annotation { "Feature Type Name" : "Feature", "Feature Type Description" : "" }
export const myFeature = defineFeature(function(context is Context, id is Id, definition is map)
    precondition{}
    {
        {
            var Q0;
            Q0=qCreatedBy(makeId("Top.planeOp"),FACE);
            var sketch = newSketch(context, id + "F0", { "sketchPlane" : qUnion([Q0])});
            skCircle(sketch, "E0", {"center": v(0, 0) * mm, "radius": 127 * mm});
            skSolve(sketch);
        }
        {
            var Q0;
            Q0 = qSketchRegion(id + "F0", true);
            extrude(context, id + "F1", {"entities" : qUnion([Q0]), "depth" : 63.5 * mm});
        }
        {
            var Q0;
            Q0=makeQuery(id+"F1.opExtrude","CAP_FACE",FACE,{"disambiguationData":[OSD([sQuery(id+"F0.wireOp",EDGE,"E0")])],"isStart":false});
            var sketch = newSketch(context, id + "F2", { "sketchPlane" : qUnion([Q0])});
            skCircle(sketch, "E1", {"center": v(0, 0) * mm, "radius": 107.95 * mm});
            skSolve(sketch);
        }
        {
            var Q0;
            Q0=makeQuery(id+"F2.imprint","IMPRINT",FACE,{"disambiguationData":[TD([[makeQuery(id+"F2.imprint","IMPRINT",EDGE,{"derivedFrom":sQuery(id+"F2.wireOp",EDGE,"E1")}),1.0]])]});
            extrude(context, id + "F3", {"entities" : qUnion([Q0]), "operationType" : NewBodyOperationType.REMOVE, "oppositeDirection" : true, "depth" : 254 * mm});
        }
        {
            var Q0;
            Q0=qCreatedBy(makeId("Front.planeOp"),FACE);
            var sketch = newSketch(context, id + "F4", { "sketchPlane" : qUnion([Q0])});
            skLineSegment(sketch, "E2", {"start": v(0, 0) * mm, "end": v(0, 63.5) * mm});
            skLineSegment(sketch, "E3", {"start": v(-127.9, 31.75) * mm, "end": v(134.22, 31.75) * mm});
            skSolve(sketch);
        }
        {
            var Q0;
            Q0=qCreatedBy(makeId("Front.planeOp"),FACE);
            var sketch = newSketch(context, id + "F5", { "sketchPlane" : qUnion([Q0])});
            skCircle(sketch, "E4.cCircle", {"center": v(0, 47.62) * mm, "radius": 12.7 * mm, "construction": true});
            skLineSegment(sketch, "E4.0", {"start": v(12.7, 47.62) * mm, "end": v(6.35, 36.63) * mm});
            skLineSegment(sketch, "E4.1", {"start": v(6.35, 36.63) * mm, "end": v(-6.35, 36.63) * mm});
            skLineSegment(sketch, "E4.2", {"start": v(-6.35, 36.63) * mm, "end": v(-12.7, 47.62) * mm});
            skLineSegment(sketch, "E4.3", {"start": v(-12.7, 47.62) * mm, "end": v(-6.35, 58.62) * mm});
            skLineSegment(sketch, "E4.4", {"start": v(-6.35, 58.62) * mm, "end": v(6.35, 58.62) * mm});
            skLineSegment(sketch, "E4.5", {"start": v(6.35, 58.62) * mm, "end": v(12.7, 47.62) * mm});
            skLineSegment(sketch, "E5.direction1", {"start": v(-6.35, 36.63) * mm, "end": v(6.35, 36.63) * mm, "construction": true});
            skPoint(sketch, "E6.orphan", {"position": v(17.46, 60.96) * mm});
            skPoint(sketch, "E7.orphan", {"position": v(9.53, 47.21) * mm});
            skPoint(sketch, "E8.orphan", {"position": v(33.34, 33.46) * mm});
            skPoint(sketch, "E9.orphan", {"position": v(41.27, 47.21) * mm});
            skPoint(sketch, "E10.orphan", {"position": v(15.87, 28.8) * mm});
            skLineSegment(sketch, "E11", {"start": v(66.67, 47.21) * mm, "end": v(66.67, 47.21) * mm});
            skPoint(sketch, "E12.orphan", {"position": v(33.34, 42.55) * mm});
            skPoint(sketch, "E13.orphan", {"position": v(9.53, 28.8) * mm});
            skLineSegment(sketch, "E14.0.1.0", {"start": v(-6.35, 4.88) * mm, "end": v(-12.7, 15.88) * mm});
            skLineSegment(sketch, "E14.0.1.1", {"start": v(-12.7, 15.88) * mm, "end": v(-6.35, 26.87) * mm});
            skLineSegment(sketch, "E14.0.1.2", {"start": v(-6.35, 26.87) * mm, "end": v(6.35, 26.87) * mm});
            skLineSegment(sketch, "E14.0.1.3", {"start": v(6.35, 26.87) * mm, "end": v(12.7, 15.87) * mm});
            skLineSegment(sketch, "E14.0.1.4", {"start": v(12.7, 15.88) * mm, "end": v(6.35, 4.88) * mm});
            skLineSegment(sketch, "E14.0.1.5", {"start": v(6.35, 4.88) * mm, "end": v(-6.35, 4.88) * mm});
            skLineSegment(sketch, "E14.direction1", {"start": v(-12.7, 47.62) * mm, "end": v(9.53, 47.62) * mm, "construction": true});
            skLineSegment(sketch, "E14.direction2", {"start": v(-12.7, 47.62) * mm, "end": v(-12.7, 15.88) * mm, "construction": true});
            skSolve(sketch);
        }
        {
            var Q0;
            Q0 = qSketchRegion(id + "F5", true);
            extrude(context, id + "F6", {"entities" : qUnion([Q0]), "operationType" : NewBodyOperationType.REMOVE, "endBound" : BoundingType.THROUGH_ALL, "depth" : 25.4 * mm});
        }
        {
            var Q0;
            Q0=makeQuery(id+"F6.boolean.opBoolean","COPY",FACE,{"derivedFrom":makeQuery(id+"F6.opExtrude","SWEPT_FACE",FACE,{"disambiguationData":[OSD([sQuery(id+"F5.wireOp",EDGE,"E4.0")])]})});
            var Q1;
            Q1=makeQuery(id+"F6.boolean.opBoolean","COPY",FACE,{"derivedFrom":makeQuery(id+"F6.opExtrude","SWEPT_FACE",FACE,{"disambiguationData":[OSD([sQuery(id+"F5.wireOp",EDGE,"E4.5")])]})});
            var Q2;
            Q2=makeQuery(id+"F6.boolean.opBoolean","COPY",FACE,{"derivedFrom":makeQuery(id+"F6.opExtrude","SWEPT_FACE",FACE,{"disambiguationData":[OSD([sQuery(id+"F5.wireOp",EDGE,"E14.0.1.3")])]})});
            var Q3;
            Q3=makeQuery(id+"F6.boolean.opBoolean","COPY",FACE,{"derivedFrom":makeQuery(id+"F6.opExtrude","SWEPT_FACE",FACE,{"disambiguationData":[OSD([sQuery(id+"F5.wireOp",EDGE,"E14.0.1.4")])]})});
            var Q4;
            Q4=makeQuery(id+"F6.boolean.opBoolean","COPY",FACE,{"derivedFrom":makeQuery(id+"F6.opExtrude","SWEPT_FACE",FACE,{"disambiguationData":[OSD([sQuery(id+"F5.wireOp",EDGE,"E4.1")])]})});
            var Q5;
            Q5=makeQuery(id+"F6.boolean.opBoolean","COPY",FACE,{"derivedFrom":makeQuery(id+"F6.opExtrude","SWEPT_FACE",FACE,{"disambiguationData":[OSD([sQuery(id+"F5.wireOp",EDGE,"E4.2")])]})});
            var Q6;
            Q6=makeQuery(id+"F6.boolean.opBoolean","COPY",FACE,{"derivedFrom":makeQuery(id+"F6.opExtrude","SWEPT_FACE",FACE,{"disambiguationData":[OSD([sQuery(id+"F5.wireOp",EDGE,"E4.3")])]})});
            var Q7;
            Q7=makeQuery(id+"F6.boolean.opBoolean","COPY",FACE,{"derivedFrom":makeQuery(id+"F6.opExtrude","SWEPT_FACE",FACE,{"disambiguationData":[OSD([sQuery(id+"F5.wireOp",EDGE,"E14.0.1.0")])]})});
            var Q8;
            Q8=makeQuery(id+"F6.boolean.opBoolean","COPY",FACE,{"derivedFrom":makeQuery(id+"F6.opExtrude","SWEPT_FACE",FACE,{"disambiguationData":[OSD([sQuery(id+"F5.wireOp",EDGE,"E14.0.1.1")])]})});
            var Q9;
            Q9=makeQuery(id+"F6.boolean.opBoolean","COPY",FACE,{"derivedFrom":makeQuery(id+"F6.opExtrude","SWEPT_FACE",FACE,{"disambiguationData":[OSD([sQuery(id+"F5.wireOp",EDGE,"E14.0.1.5")])]})});
            var Q10;
            Q10=makeQuery(id+"F6.boolean.opBoolean","COPY",FACE,{"derivedFrom":makeQuery(id+"F6.opExtrude","SWEPT_FACE",FACE,{"disambiguationData":[OSD([sQuery(id+"F5.wireOp",EDGE,"E14.0.1.2")])]})});
            var Q11;
            Q11=makeQuery(id+"F6.boolean.opBoolean","COPY",FACE,{"derivedFrom":makeQuery(id+"F6.opExtrude","SWEPT_FACE",FACE,{"disambiguationData":[OSD([sQuery(id+"F5.wireOp",EDGE,"E4.4")])]})});
            var Q12;
            Q12=sQuery(id+"F4.wireOp",EDGE,"E2");
            circularPattern(context, id + "F7", {"patternType" : PatternType.FACE, "faces" : qUnion([Q0, Q1, Q2, Q3, Q4, Q5, Q6, Q7, Q8, Q9, Q10, Q11]), "axis" : qUnion([Q12]), "angle" : 360 * degree, "instanceCount" : 14, "equalSpace" : true});
        }
        {
            var Q0;
            Q0=makeQuery(id+"F1.opExtrude","CAP_FACE",FACE,{"disambiguationData":[OSD([sQuery(id+"F0.wireOp",EDGE,"E0")])],"isStart":false});
            var Q1;
            Q1=makeQuery(id+"F1.opExtrude","CAP_FACE",FACE,{"disambiguationData":[OSD([sQuery(id+"F0.wireOp",EDGE,"E0")])],"isStart":true});
            cPlane(context, id + "F8", {"entities" : qUnion([Q0, Q1]), "cplaneType" : CPlaneType.MID_PLANE, "offset" : 25.4 * mm, "width" : 152.4 * mm, "height" : 152.4 * mm});
        }
        {
            var Q0;
            Q0=qCreatedBy(id+"F8.planeOp",FACE);
            var sketch = newSketch(context, id + "F9", { "sketchPlane" : qUnion([Q0])});
            skCircle(sketch, "E15", {"center": v(0, 0) * mm, "radius": 120.06 * mm});
            skLineSegment(sketch, "E16", {"start": v(0, 0) * mm, "end": v(190.3, 0) * mm});
            skLineSegment(sketch, "E17", {"start": v(190.3, 0) * mm, "end": v(0, 0) * mm});
            skLineSegment(sketch, "E18", {"start": v(169.78, 81.76) * mm, "end": v(0, 0) * mm});
            skLineSegment(sketch, "E19", {"start": v(108.17, 52.1) * mm, "end": v(89.15, 91.6) * mm});
            skPoint(sketch, "E20", {"position": v(108.17, 52.1) * mm});
            skSolve(sketch);
        }
        {
            var Q0;
            Q0=sQuery(id+"F9.wireOp",VERTEX,"E20");
            var Q1;
            Q1=sQuery(id+"F9.wireOp",EDGE,"E18");
            cPlane(context, id + "F10", {"entities" : qUnion([Q0, Q1]), "cplaneType" : CPlaneType.LINE_POINT, "offset" : 25.4 * mm, "width" : 152.4 * mm, "height" : 152.4 * mm});
        }
        {
            var Q0;
            Q0=qCreatedBy(id+"F10.planeOp",FACE);
            var sketch = newSketch(context, id + "F11", { "sketchPlane" : qUnion([Q0])});
            skCircle(sketch, "E21.cCircle", {"center": v(0, 31.75) * mm, "radius": 12.7 * mm, "construction": true});
            skLineSegment(sketch, "E21.0", {"start": v(-12.7, 31.75) * mm, "end": v(-6.35, 42.75) * mm});
            skLineSegment(sketch, "E21.1", {"start": v(-6.35, 42.75) * mm, "end": v(6.35, 42.75) * mm});
            skLineSegment(sketch, "E21.2", {"start": v(6.35, 42.75) * mm, "end": v(12.7, 31.75) * mm});
            skLineSegment(sketch, "E21.3", {"start": v(12.7, 31.75) * mm, "end": v(6.35, 20.75) * mm});
            skLineSegment(sketch, "E21.4", {"start": v(6.35, 20.75) * mm, "end": v(-6.35, 20.75) * mm});
            skLineSegment(sketch, "E21.5", {"start": v(-6.35, 20.75) * mm, "end": v(-12.7, 31.75) * mm});
            skLineSegment(sketch, "E22.0.1.0", {"start": v(-6.35, 74.5) * mm, "end": v(6.35, 74.5) * mm, "construction": true});
            skLineSegment(sketch, "E22.0.1.1", {"start": v(-12.7, 63.5) * mm, "end": v(-6.35, 74.5) * mm, "construction": true});
            skLineSegment(sketch, "E22.0.1.2", {"start": v(-6.35, 52.5) * mm, "end": v(-9.88, 58.62) * mm});
            skLineSegment(sketch, "E22.0.1.3", {"start": v(6.35, 52.5) * mm, "end": v(-6.35, 52.5) * mm});
            skLineSegment(sketch, "E22.0.1.4", {"start": v(9.88, 58.62) * mm, "end": v(6.35, 52.5) * mm});
            skLineSegment(sketch, "E22.0.1.5", {"start": v(6.35, 74.5) * mm, "end": v(12.7, 63.5) * mm, "construction": true});
            skLineSegment(sketch, "E22.direction1", {"start": v(-6.35, 42.75) * mm, "end": v(17.46, 42.75) * mm, "construction": true});
            skLineSegment(sketch, "E22.direction2", {"start": v(-6.35, 42.75) * mm, "end": v(-6.35, 74.5) * mm, "construction": true});
            skLineSegment(sketch, "E23.0.1.0", {"start": v(6.35, 11) * mm, "end": v(9.88, 4.88) * mm});
            skLineSegment(sketch, "E23.0.1.1", {"start": v(-9.88, 4.88) * mm, "end": v(-6.35, 11) * mm});
            skLineSegment(sketch, "E23.direction1", {"start": v(12.7, 31.75) * mm, "end": v(41.27, 31.75) * mm, "construction": true});
            skLineSegment(sketch, "E23.direction2", {"start": v(12.7, 31.75) * mm, "end": v(12.7, 0) * mm, "construction": true});
            skLineSegment(sketch, "E24", {"start": v(6.35, 11) * mm, "end": v(-6.35, 11) * mm});
            skLineSegment(sketch, "E25", {"start": v(9.88, 58.62) * mm, "end": v(-9.88, 58.62) * mm});
            skLineSegment(sketch, "E26", {"start": v(9.88, 4.88) * mm, "end": v(-9.88, 4.88) * mm});
            skSolve(sketch);
        }
        {
            var Q0;
            Q0=qCreatedBy(makeId("Front.planeOp"),FACE);
            var sketch = newSketch(context, id + "F12", { "sketchPlane" : qUnion([Q0])});
            skLineSegment(sketch, "E27", {"start": v(145.81, 63.5) * mm, "end": v(145.81, 63.5) * mm});
            skLineSegment(sketch, "E28", {"start": v(0, 0) * mm, "end": v(0, 93.67) * mm, "construction": true});
            skSolve(sketch);
        }
        {
            var Q0;
            Q0 = qSketchRegion(id + "F11", true);
            extrude(context, id + "F13", {"entities" : qUnion([Q0]), "operationType" : NewBodyOperationType.REMOVE, "endBound" : BoundingType.SYMMETRIC, "depth" : 381 * mm});
        }
        {
            var Q0;
            Q0=makeQuery(id+"F13.boolean.opBoolean","COPY",FACE,{"derivedFrom":makeQuery(id+"F13.opExtrude","SWEPT_FACE",FACE,{"disambiguationData":[OSD([sQuery(id+"F11.wireOp",EDGE,"E21.3")])]})});
            var Q1;
            Q1=makeQuery(id+"F13.boolean.opBoolean","COPY",FACE,{"derivedFrom":makeQuery(id+"F13.opExtrude","SWEPT_FACE",FACE,{"disambiguationData":[OSD([sQuery(id+"F11.wireOp",EDGE,"E21.2")])]})});
            var Q2;
            Q2=makeQuery(id+"F13.boolean.opBoolean","COPY",FACE,{"derivedFrom":makeQuery(id+"F13.opExtrude","SWEPT_FACE",FACE,{"disambiguationData":[OSD([sQuery(id+"F11.wireOp",EDGE,"E22.0.1.4")])]})});
            var Q3;
            Q3=makeQuery(id+"F13.boolean.opBoolean","COPY",FACE,{"derivedFrom":makeQuery(id+"F13.opExtrude","SWEPT_FACE",FACE,{"disambiguationData":[OSD([sQuery(id+"F11.wireOp",EDGE,"E22.0.1.3")])]})});
            var Q4;
            Q4=makeQuery(id+"F13.boolean.opBoolean","COPY",FACE,{"derivedFrom":makeQuery(id+"F13.opExtrude","SWEPT_FACE",FACE,{"disambiguationData":[OSD([sQuery(id+"F11.wireOp",EDGE,"E21.4")])]})});
            var Q5;
            Q5=makeQuery(id+"F13.boolean.opBoolean","COPY",FACE,{"derivedFrom":makeQuery(id+"F13.opExtrude","SWEPT_FACE",FACE,{"disambiguationData":[OSD([sQuery(id+"F11.wireOp",EDGE,"E26")])]})});
            var Q6;
            Q6=makeQuery(id+"F13.boolean.opBoolean","COPY",FACE,{"derivedFrom":makeQuery(id+"F13.opExtrude","SWEPT_FACE",FACE,{"disambiguationData":[OSD([sQuery(id+"F11.wireOp",EDGE,"E22.0.1.2")])]})});
            var Q7;
            Q7=makeQuery(id+"F13.boolean.opBoolean","COPY",FACE,{"derivedFrom":makeQuery(id+"F13.opExtrude","SWEPT_FACE",FACE,{"disambiguationData":[OSD([sQuery(id+"F11.wireOp",EDGE,"E21.0")])]})});
            var Q8;
            Q8=makeQuery(id+"F13.boolean.opBoolean","COPY",FACE,{"derivedFrom":makeQuery(id+"F13.opExtrude","SWEPT_FACE",FACE,{"disambiguationData":[OSD([sQuery(id+"F11.wireOp",EDGE,"E21.5")])]})});
            var Q9;
            Q9=makeQuery(id+"F13.boolean.opBoolean","COPY",FACE,{"derivedFrom":makeQuery(id+"F13.opExtrude","SWEPT_FACE",FACE,{"disambiguationData":[OSD([sQuery(id+"F11.wireOp",EDGE,"E23.0.1.1")])]})});
            var Q10;
            Q10=makeQuery(id+"F13.boolean.opBoolean","COPY",FACE,{"derivedFrom":makeQuery(id+"F13.opExtrude","SWEPT_FACE",FACE,{"disambiguationData":[OSD([sQuery(id+"F11.wireOp",EDGE,"E24")])]})});
            var Q11;
            Q11=makeQuery(id+"F13.boolean.opBoolean","COPY",FACE,{"derivedFrom":makeQuery(id+"F13.opExtrude","SWEPT_FACE",FACE,{"disambiguationData":[OSD([sQuery(id+"F11.wireOp",EDGE,"E23.0.1.0")])]})});
            var Q12;
            Q12=makeQuery(id+"F13.boolean.opBoolean","COPY",FACE,{"derivedFrom":makeQuery(id+"F13.opExtrude","SWEPT_FACE",FACE,{"disambiguationData":[OSD([sQuery(id+"F11.wireOp",EDGE,"E25")])]})});
            var Q13;
            Q13=makeQuery(id+"F13.boolean.opBoolean","COPY",FACE,{"derivedFrom":makeQuery(id+"F13.opExtrude","SWEPT_FACE",FACE,{"disambiguationData":[OSD([sQuery(id+"F11.wireOp",EDGE,"E21.1")])]})});
            var Q14;
            Q14=sQuery(id+"F12.wireOp",EDGE,"E28");
            circularPattern(context, id + "F14", {"patternType" : PatternType.FACE, "faces" : qUnion([Q0, Q1, Q2, Q3, Q4, Q5, Q6, Q7, Q8, Q9, Q10, Q11, Q12, Q13]), "axis" : qUnion([Q14]), "angle" : 360 * degree, "instanceCount" : 14, "equalSpace" : true});
        }
        {
            var Q0;
            Q0=qCreatedBy(makeId("Right.planeOp"),FACE);
            var sketch = newSketch(context, id + "F15", { "sketchPlane" : qUnion([Q0])});
            skLineSegment(sketch, "E29", {"start": v(0, 0) * mm, "end": v(127, 0) * mm, "construction": true});
            skLineSegment(sketch, "E30", {"start": v(127, 0) * mm, "end": v(127, 63.5) * mm});
            skLineSegment(sketch, "E31", {"start": v(127, 63.5) * mm, "end": v(120.65, 63.5) * mm});
            skLineSegment(sketch, "E32", {"start": v(127, 0) * mm, "end": v(120.65, 0) * mm});
            skLineSegment(sketch, "E33", {"start": v(88.17, 31.75) * mm, "end": v(176.04, 31.75) * mm, "construction": true});
            skArc(sketch, "E34", {"start": v(120.65, 0) * mm, "mid": v(127, 31.75) * mm, "end": v(120.65, 63.5) * mm});
            skSolve(sketch);
        }
        {
            var Q0;
            Q0 = qSketchRegion(id + "F15", true);
            var Q1;
            Q1=sQuery(id+"F4.wireOp",EDGE,"E2");
            revolve(context, id + "F16", {"operationType" : NewBodyOperationType.REMOVE, "entities" : qUnion([Q0]), "axis" : qUnion([Q1]), "revolveType" : RevolveType.FULL, "oppositeDirection" : true});
        }
        {
            var Q0;
            Q0=makeQuery(id+"F3.boolean.opBoolean","COPY",EDGE,{"derivedFrom":makeQuery(id+"F3.opExtrude","CAP_EDGE",EDGE,{"disambiguationData":[OSD([sQuery(id+"F2.wireOp",EDGE,"E1")])],"isStart":true})});
            var Q1;
            Q1=makeQuery(id+"F3.boolean.opBoolean","INTERSECT",EDGE,{"derivedFrom":[makeQuery(id+"F1.opExtrude","CAP_FACE",FACE,{"disambiguationData":[OSD([sQuery(id+"F0.wireOp",EDGE,"E0")])],"isStart":true}),makeQuery(id+"F3.opExtrude","SWEPT_FACE",FACE,{"disambiguationData":[OSD([sQuery(id+"F2.wireOp",EDGE,"E1")])]})]});
            var Q2;
            Q2=makeQuery(id+"F16.boolean.opBoolean","COPY",EDGE,{"derivedFrom":makeQuery(id+"F16.opRevolve","SWEPT_EDGE",EDGE,{"disambiguationData":[OSD([sQuery(id+"F15.wireOp",EDGE,"E31"),sQuery(id+"F15.wireOp",EDGE,"E34")])]})});
            var Q3;
            Q3=makeQuery(id+"F16.boolean.opBoolean","COPY",EDGE,{"derivedFrom":makeQuery(id+"F16.opRevolve","SWEPT_EDGE",EDGE,{"disambiguationData":[OSD([sQuery(id+"F15.wireOp",EDGE,"E32"),sQuery(id+"F15.wireOp",EDGE,"E34")])]})});
            fillet(context, id + "F17", {"entities" : qUnion([Q0, Q1, Q2, Q3]), "radius" : 5.08 * mm, "tangentPropagation" : true, "allowEdgeOverflow" : false});
        }
    });